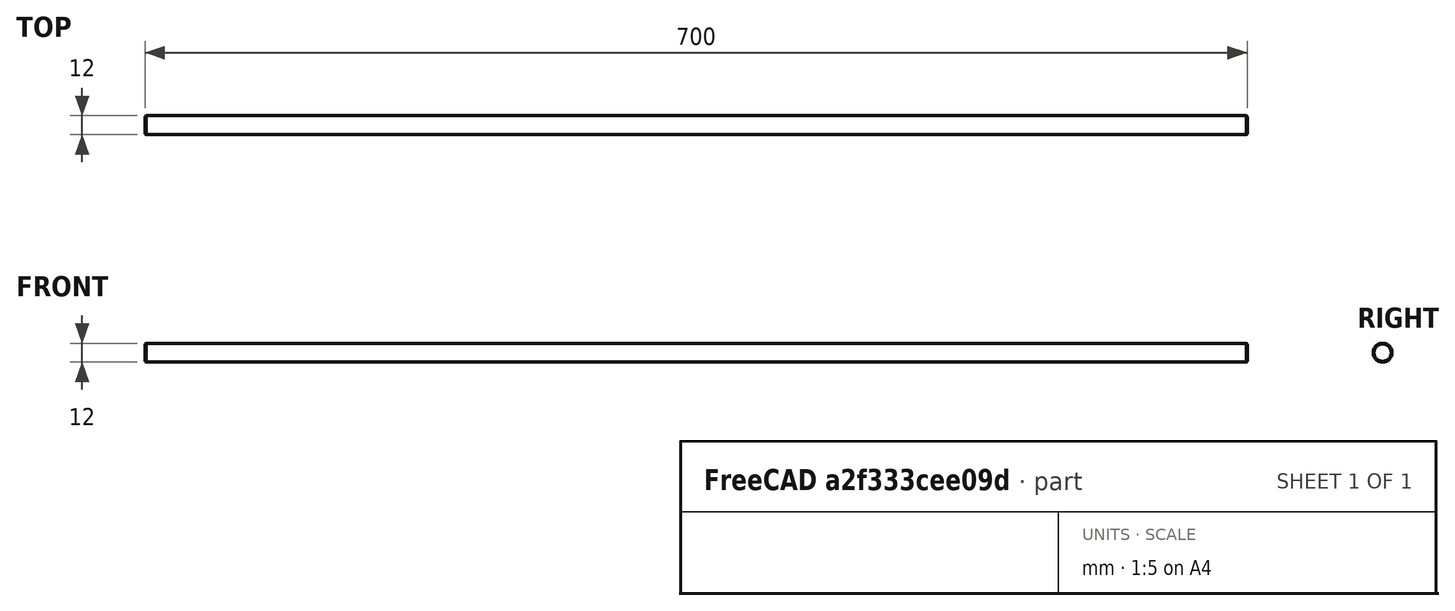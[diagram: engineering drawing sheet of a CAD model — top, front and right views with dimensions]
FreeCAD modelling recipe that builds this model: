
FCSTD DOCUMENT  (FreeCAD 0.15R4671 (Git))
Label: rod-700
License: All rights reserved
LicenseURL: http://en.wikipedia.org/wiki/All_rights_reserved
objects: Sketcher::SketchObject×1, PartDesign::Pad×1, PartDesign::Chamfer×1
note: 4 computed .brp shape members not serialized (recipe doc carries the construction recipe); baked Part::Feature solids carry a one-line shape summary decoded from their .brp

FEATURE [Sketcher::SketchObject] Sketch  label="rod-sketch"
  Placement = pos=(0,0,0) rot=(0.57735,0.57735,0.57735;2.0944rad)
  sketch-geometry (1):
    g0: Circle CenterX=0 CenterY=0 CenterZ=0 NormalX=0 NormalY=0 NormalZ=1 Radius=6
  constraints (2):
    c: Coincident(g0,g-1)
    c: Radius(g0) = 6
FEATURE [PartDesign::Pad] Pad  label="rod"
  Length = 700
  Length2 = 100
  Midplane = true
  Placement = pos=(0,0,0) rot=(0.57735,0.57735,0.57735;2.0944rad)
  Sketch = -> Sketch
  Type = 0
FEATURE [PartDesign::Chamfer] Chamfer  label="rod-700"
  Base = -> Pad [Edge3,Edge2]
  Placement = pos=(0,0,0) rot=(0.57735,0.57735,0.57735;2.0944rad)
  Size = 0.5
